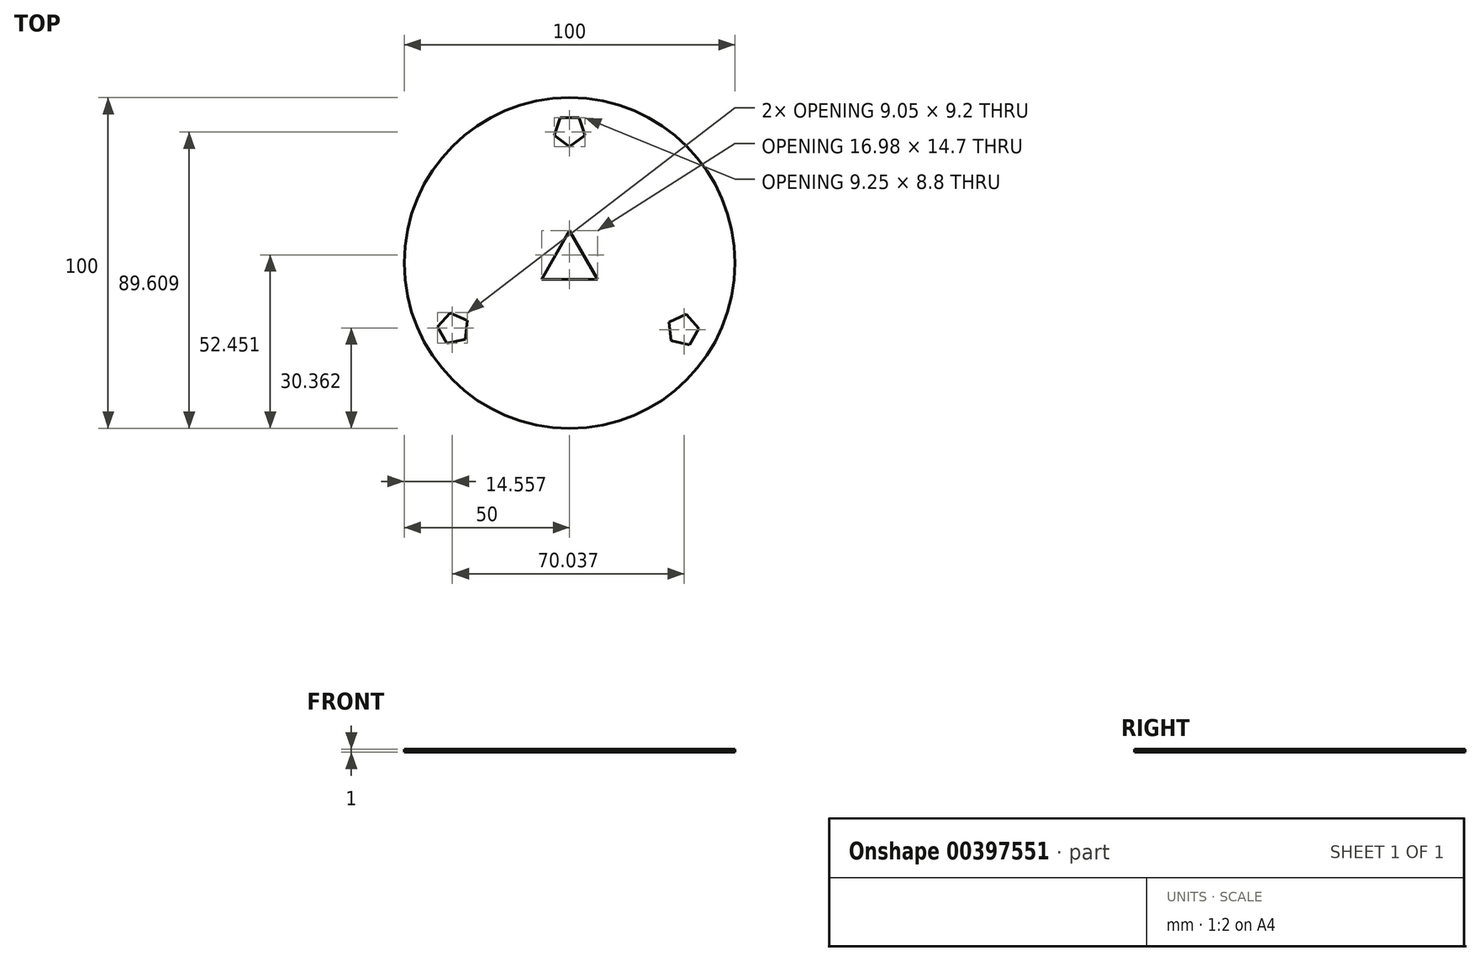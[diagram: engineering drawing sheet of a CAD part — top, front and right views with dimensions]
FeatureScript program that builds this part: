
annotation { "Feature Type Name" : "Feature", "Feature Type Description" : "" }
export const myFeature = defineFeature(function(context is Context, id is Id, definition is map)
    precondition{}
    {
        {
            var Q0;
            Q0=qCreatedBy(makeId("Top.planeOp"),FACE);
            var sketch = newSketch(context, id + "F0", { "sketchPlane" : qUnion([Q0])});
            skCircle(sketch, "E0", {"center": v(0, 0) * mm, "radius": 50 * mm});
            skCircle(sketch, "E1.cCircle", {"center": v(0, 40.07) * mm, "radius": 3.93 * mm, "construction": true});
            skLineSegment(sketch, "E1.0", {"start": v(4.62, 38.57) * mm, "end": v(0, 35.21) * mm});
            skLineSegment(sketch, "E1.1", {"start": v(0, 35.21) * mm, "end": v(-4.62, 38.57) * mm});
            skLineSegment(sketch, "E1.2", {"start": v(-4.62, 38.57) * mm, "end": v(-2.86, 44) * mm});
            skLineSegment(sketch, "E1.3", {"start": v(-2.86, 44) * mm, "end": v(2.86, 44) * mm});
            skLineSegment(sketch, "E1.4", {"start": v(2.86, 44) * mm, "end": v(4.62, 38.57) * mm});
            skPoint(sketch, "E1.0.midPoint", {"position": v(2.31, 36.9) * mm});
            skCircle(sketch, "E2.1.0", {"center": v(-35.13, -19.8) * mm, "radius": 3.93 * mm, "construction": true});
            skLineSegment(sketch, "E2.1.1", {"start": v(-36.14, -15.04) * mm, "end": v(-30.92, -17.36) * mm});
            skLineSegment(sketch, "E2.1.2", {"start": v(-30.92, -17.36) * mm, "end": v(-31.52, -23.05) * mm});
            skLineSegment(sketch, "E2.1.3", {"start": v(-31.52, -23.05) * mm, "end": v(-37.1, -24.24) * mm});
            skLineSegment(sketch, "E2.1.4", {"start": v(-37.1, -24.24) * mm, "end": v(-39.97, -19.29) * mm});
            skLineSegment(sketch, "E2.1.5", {"start": v(-39.97, -19.29) * mm, "end": v(-36.14, -15.04) * mm});
            skPoint(sketch, "E2.1.6", {"position": v(-33.53, -16.2) * mm});
            skCircle(sketch, "E2.2.0", {"center": v(34.28, -20.28) * mm, "radius": 3.93 * mm, "construction": true});
            skLineSegment(sketch, "E2.2.1", {"start": v(30.67, -23.54) * mm, "end": v(30.07, -17.85) * mm});
            skLineSegment(sketch, "E2.2.2", {"start": v(30.07, -17.85) * mm, "end": v(35.3, -15.53) * mm});
            skLineSegment(sketch, "E2.2.3", {"start": v(35.3, -15.53) * mm, "end": v(39.12, -19.78) * mm});
            skLineSegment(sketch, "E2.2.4", {"start": v(39.12, -19.78) * mm, "end": v(36.26, -24.73) * mm});
            skLineSegment(sketch, "E2.2.5", {"start": v(36.26, -24.73) * mm, "end": v(30.67, -23.54) * mm});
            skPoint(sketch, "E2.2.6", {"position": v(30.37, -20.7) * mm});
            skPoint(sketch, "E2.center", {"position": v(-0.28, 0) * mm});
            skCircle(sketch, "E3.cCircle", {"center": v(0, 0) * mm, "radius": 4.9 * mm, "construction": true});
            skLineSegment(sketch, "E3.0", {"start": v(-8.49, -4.9) * mm, "end": v(0, 9.8) * mm});
            skLineSegment(sketch, "E3.1", {"start": v(0, 9.8) * mm, "end": v(8.49, -4.9) * mm});
            skLineSegment(sketch, "E3.2", {"start": v(8.49, -4.9) * mm, "end": v(-8.49, -4.9) * mm});
            skPoint(sketch, "E3.0.midPoint", {"position": v(-4.24, 2.45) * mm});
            skSolve(sketch);
        }
        {
            var Q0;
            Q0=makeQuery(id+"F0.imprint","IMPRINT",FACE,{"disambiguationData":[TD([[makeQuery(id+"F0.imprint","IMPRINT",EDGE,{"derivedFrom":sQuery(id+"F0.wireOp",EDGE,"E0")}),1.0]])]});
            extrude(context, id + "F1", {"entities" : qUnion([Q0]), "depth" : 1 * mm});
        }
    });
